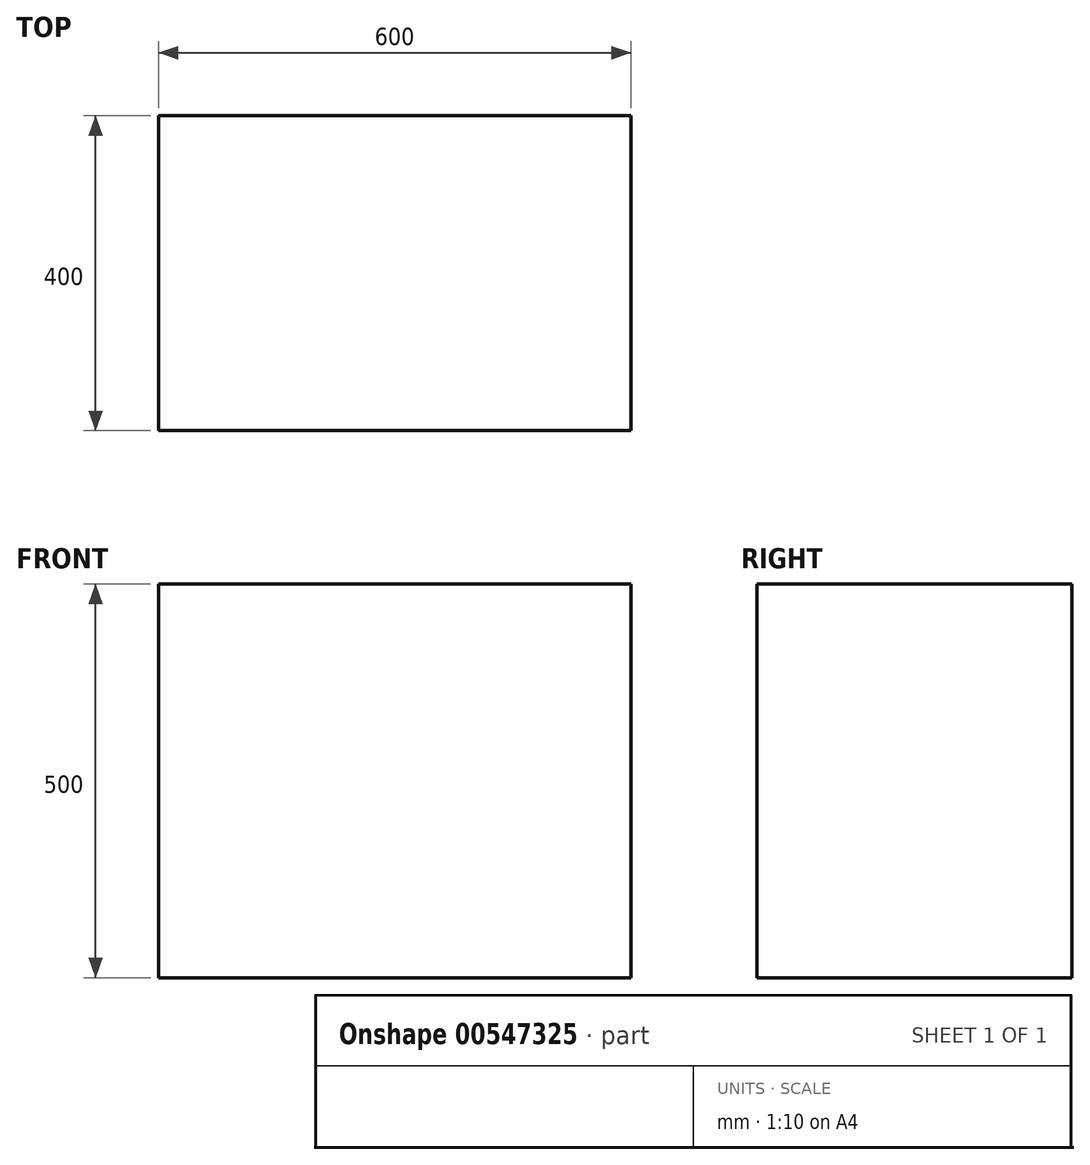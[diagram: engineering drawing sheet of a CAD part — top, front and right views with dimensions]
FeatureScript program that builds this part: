
annotation { "Feature Type Name" : "Feature", "Feature Type Description" : "" }
export const myFeature = defineFeature(function(context is Context, id is Id, definition is map)
    precondition{}
    {
        {
            var Q0;
            Q0=qCreatedBy(makeId("Top.planeOp"),FACE);
            var sketch = newSketch(context, id + "F0", { "sketchPlane" : qUnion([Q0])});
            skLineSegment(sketch, "E0.bottom", {"start": v(300, -200) * mm, "end": v(-300, -200) * mm});
            skLineSegment(sketch, "E0.top", {"start": v(300, 200) * mm, "end": v(-300, 200) * mm});
            skLineSegment(sketch, "E0.left", {"start": v(300, -200) * mm, "end": v(300, 200) * mm});
            skLineSegment(sketch, "E0.right", {"start": v(-300, -200) * mm, "end": v(-300, 200) * mm});
            skPoint(sketch, "E0.middle", {"position": v(0, 0) * mm});
            skSolve(sketch);
        }
        {
            var Q0;
            Q0=makeQuery(id+"F0.imprint","IMPRINT",FACE,{"disambiguationData":[TD([[makeQuery(id+"F0.imprint","IMPRINT",EDGE,{"derivedFrom":sQuery(id+"F0.wireOp",EDGE,"E0.bottom")}),-1.0]])]});
            extrude(context, id + "F1", {"entities" : qUnion([Q0]), "depth" : 500 * mm, "offsetDistance" : 25 * mm});
        }
    });
